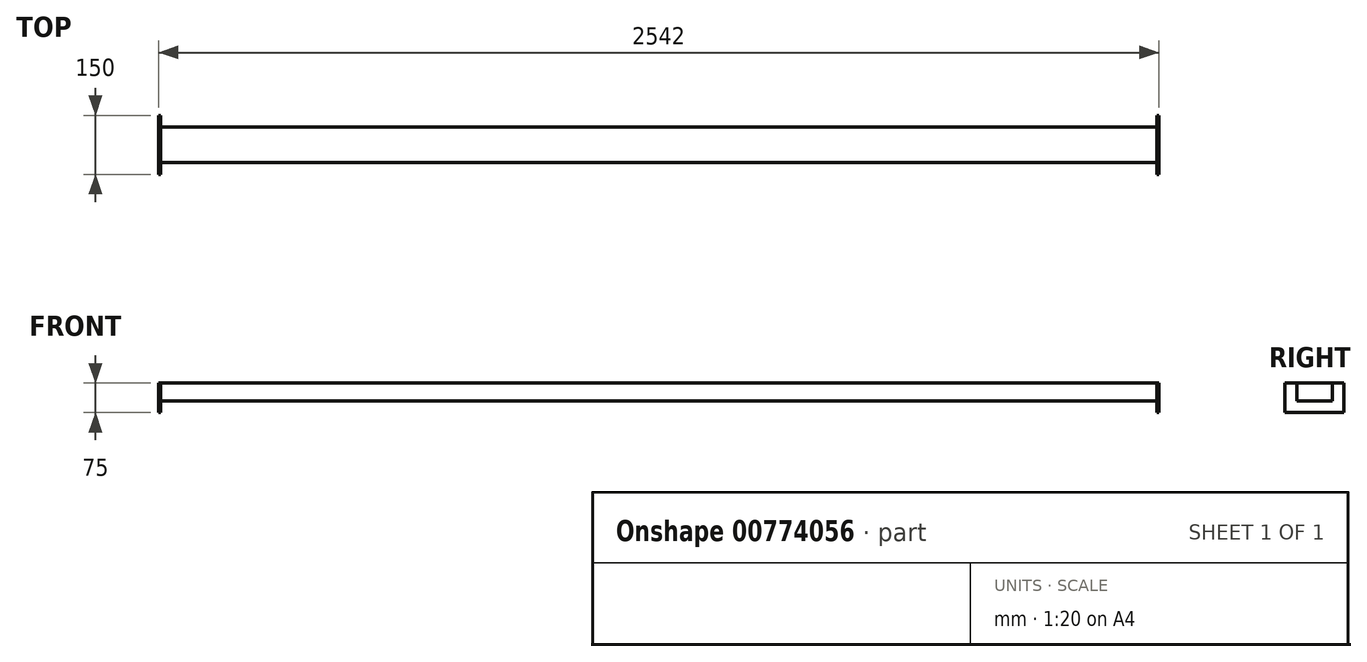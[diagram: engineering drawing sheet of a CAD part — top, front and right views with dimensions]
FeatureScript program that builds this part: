
annotation { "Feature Type Name" : "Feature", "Feature Type Description" : "" }
export const myFeature = defineFeature(function(context is Context, id is Id, definition is map)
    precondition{}
    {
        {
            var Q0;
            Q0=qCreatedBy(makeId("Top.planeOp"),FACE);
            var sketch = newSketch(context, id + "F0", { "sketchPlane" : qUnion([Q0])});
            skLineSegment(sketch, "E0", {"start": v(0, 0) * mm, "end": v(2532, 0) * mm});
            skLineSegment(sketch, "E1", {"start": v(2532, 0) * mm, "end": v(2532, 90) * mm});
            skLineSegment(sketch, "E2", {"start": v(2532, 90) * mm, "end": v(0, 90) * mm});
            skLineSegment(sketch, "E3", {"start": v(0, 90) * mm, "end": v(0, 0) * mm});
            skSolve(sketch);
        }
        {
            var Q0;
            Q0=makeQuery(id+"F0.imprint","IMPRINT",FACE,{"disambiguationData":[TD([[makeQuery(id+"F0.imprint","IMPRINT",EDGE,{"derivedFrom":sQuery(id+"F0.wireOp",EDGE,"E0")}),1.0]])]});
            extrude(context, id + "F1", {"entities" : qUnion([Q0]), "depth" : 45 * mm, "offsetDistance" : 25 * mm});
        }
        {
            var Q0;
            Q0=makeQuery(id+"F1.opExtrude","SWEPT_FACE",FACE,{"disambiguationData":[OSD([sQuery(id+"F0.wireOp",EDGE,"E1")])]});
            var sketch = newSketch(context, id + "F2", { "sketchPlane" : qUnion([Q0])});
            skLineSegment(sketch, "E4", {"start": v(120, 45) * mm, "end": v(120, -30) * mm});
            skLineSegment(sketch, "E5", {"start": v(120, -30) * mm, "end": v(-30, -30) * mm});
            skLineSegment(sketch, "E6", {"start": v(-30, -30) * mm, "end": v(-30, 45) * mm});
            skLineSegment(sketch, "E7", {"start": v(120, 45) * mm, "end": v(90, 45) * mm});
            skLineSegment(sketch, "E8", {"start": v(90, 45) * mm, "end": v(0, 45) * mm});
            skLineSegment(sketch, "E9", {"start": v(0, 45) * mm, "end": v(-30, 45) * mm});
            skSolve(sketch);
        }
        {
            var Q0;
            {var subQ3=sQuery(id+"F2.wireOp",EDGE,"E4");Q0=makeQuery(id+"F2.imprint","IMPRINT",FACE,{"disambiguationData":[TD([[makeQuery(id+"F2.imprint","IMPRINT",EDGE,{"derivedFrom":subQ3}),-1.0]])]});}
            var Q1;
            Q1=makeQuery(id+"F1.opExtrude","SWEPT_FACE",FACE,{"disambiguationData":[OSD([sQuery(id+"F0.wireOp",EDGE,"E3")])]});
            extrude(context, id + "F3", {"entities" : qUnion([Q0, Q1]), "operationType" : NewBodyOperationType.ADD, "depth" : 5 * mm, "offsetDistance" : 25 * mm});
        }
        {
            var Q0;
            Q0=makeQuery(id+"F1.opExtrude","SWEPT_FACE",FACE,{"disambiguationData":[OSD([sQuery(id+"F0.wireOp",EDGE,"E3")])]});
            var Q1;
            Q1=makeQuery(id+"F1.opExtrude","SWEPT_FACE",FACE,{"disambiguationData":[OSD([sQuery(id+"F0.wireOp",EDGE,"E1")])]});
            cPlane(context, id + "F4", {"entities" : qUnion([Q0, Q1]), "cplaneType" : CPlaneType.MID_PLANE, "offset" : 25 * mm, "width" : 150 * mm, "height" : 150 * mm});
        }
        {
            var Q0;
            {var subQ0=sQuery(id+"F0.wireOp",EDGE,"E2");var subQ1=sQuery(id+"F0.wireOp",EDGE,"E1");var subQ2=sQuery(id+"F0.wireOp",EDGE,"E0");var subQ3=sQuery(id+"F0.wireOp",EDGE,"E3");Q0=makeQuery(id+"F3.boolean.opBoolean","MERGE",BODY,{"derivedFrom":[makeQuery(id+"F1.opExtrude","SWEPT_BODY",BODY,{"disambiguationData":[OSD([subQ2,subQ1,subQ0,subQ3])]}),makeQuery(id+"F3.opExtrude","SWEPT_BODY",BODY,{"disambiguationData":[OSD([subQ3])]}),makeQuery(id+"F3.opExtrude","SWEPT_BODY",BODY,{"disambiguationData":[OSD([subQ2,subQ1,subQ0,sQuery(id+"F2.wireOp",EDGE,"E4"),sQuery(id+"F2.wireOp",EDGE,"E5"),sQuery(id+"F2.wireOp",EDGE,"E6"),sQuery(id+"F2.wireOp",EDGE,"TzBoDAN4-QSZm-8VdA-rFvj-7zqyz27oseEM")])]})]});}
            var Q1;
            Q1=qCreatedBy(id+"F4.planeOp",FACE);
            mirror(context, id + "F5", {"entities" : qUnion([Q0]), "mirrorPlane" : qUnion([Q1])});
        }
        {
            var Q0;
            Q0=makeQuery(id+"F1.opExtrude","SWEPT_FACE",FACE,{"disambiguationData":[OSD([sQuery(id+"F0.wireOp",EDGE,"E3")])]});
            extrude(context, id + "F6", {"entities" : qUnion([Q0]), "depth" : 5 * mm, "offsetDistance" : 25 * mm});
        }
        {
            var Q0;
            Q0=makeQuery(id+"F1.opExtrude","SWEPT_FACE",FACE,{"disambiguationData":[OSD([sQuery(id+"F0.wireOp",EDGE,"E1")])]});
            extrude(context, id + "F7", {"entities" : qUnion([Q0]), "depth" : 5 * mm, "offsetDistance" : 25 * mm});
        }
    });
